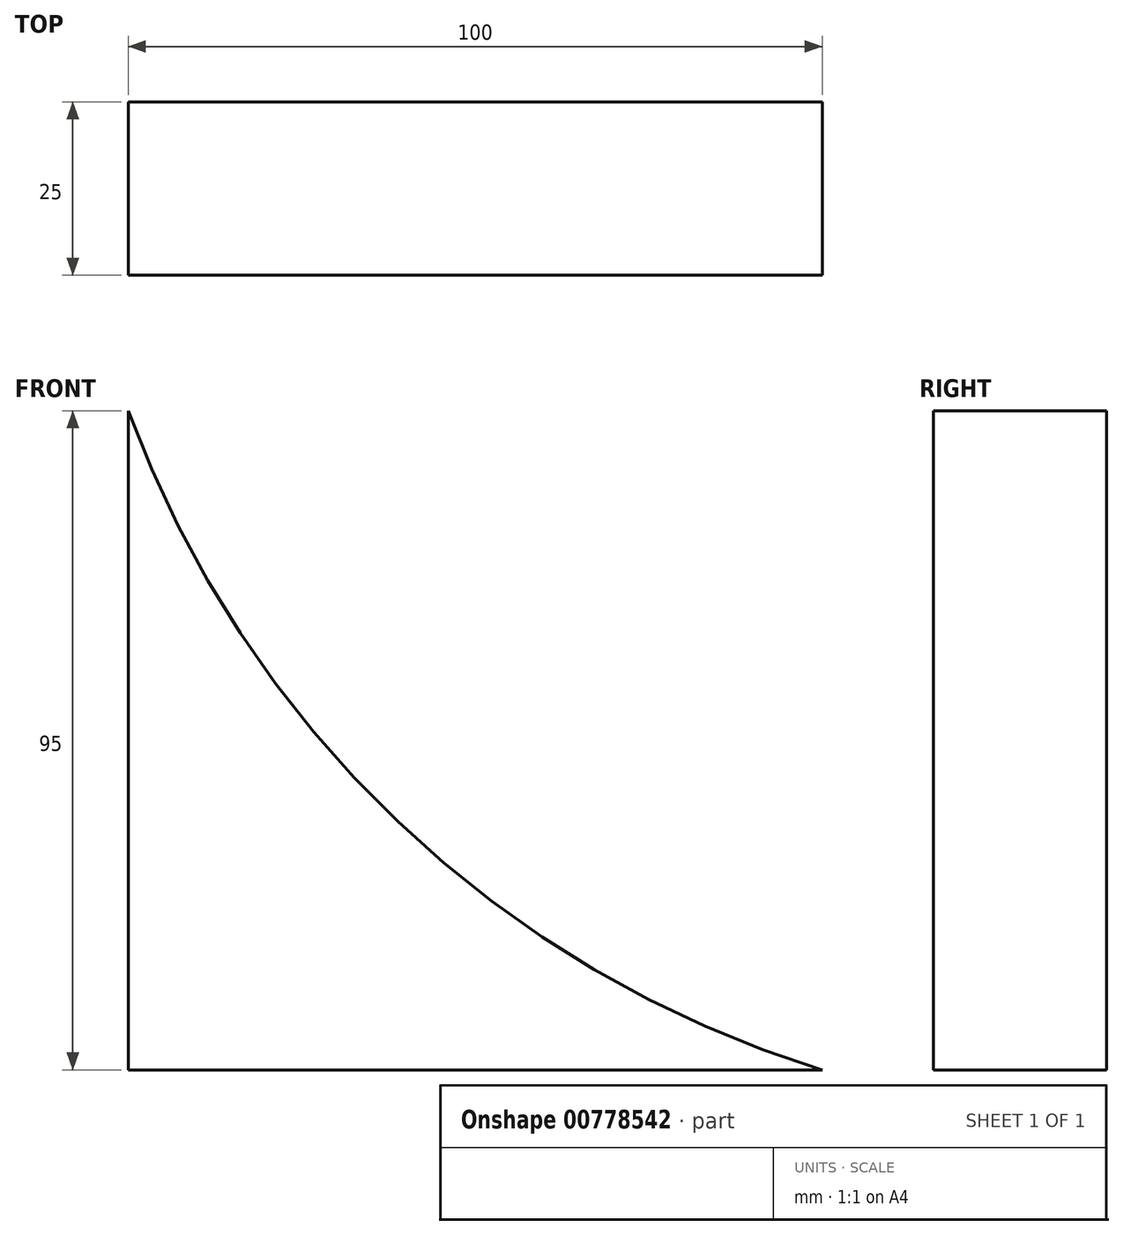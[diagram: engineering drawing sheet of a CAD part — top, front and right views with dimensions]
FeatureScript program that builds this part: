
annotation { "Feature Type Name" : "Feature", "Feature Type Description" : "" }
export const myFeature = defineFeature(function(context is Context, id is Id, definition is map)
    precondition{}
    {
        {
            var Q0;
            Q0=qCreatedBy(makeId("Front.planeOp"),FACE);
            var sketch = newSketch(context, id + "F0", { "sketchPlane" : qUnion([Q0])});
            skLineSegment(sketch, "E0", {"start": v(0, 0) * mm, "end": v(0, 95) * mm});
            skLineSegment(sketch, "E1", {"start": v(100, 0) * mm, "end": v(0, 0) * mm});
            skArc(sketch, "E2", {"start": v(0, 95) * mm, "mid": v(38.85, 35.76) * mm, "end": v(100, 0) * mm});
            skLineSegment(sketch, "E3.left", {"start": v(0, 95) * mm, "end": v(0, 0) * mm});
            skSolve(sketch);
        }
        {
            var Q0;
            Q0=makeQuery(id+"F0.imprint","IMPRINT",FACE,{"disambiguationData":[TD([[makeQuery(id+"F0.imprint","IMPRINT",EDGE,{"derivedFrom":sQuery(id+"F0.wireOp",EDGE,"E1")}),-1.0]])]});
            extrude(context, id + "F1", {"entities" : qUnion([Q0]), "depth" : 25 * mm, "offsetDistance" : 25 * mm});
        }
    });
